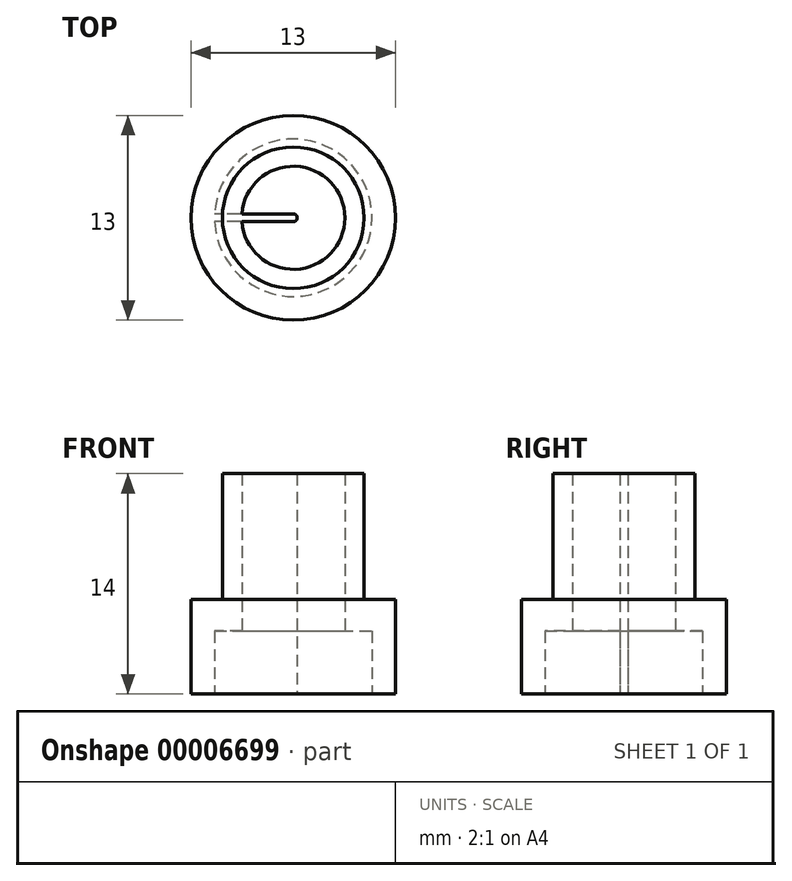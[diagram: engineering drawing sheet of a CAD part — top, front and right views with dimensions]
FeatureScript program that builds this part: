
annotation { "Feature Type Name" : "Feature", "Feature Type Description" : "" }
export const myFeature = defineFeature(function(context is Context, id is Id, definition is map)
    precondition{}
    {
        {
            var Q0;
            Q0=qCreatedBy(makeId("Top.planeOp"),FACE);
            var sketch = newSketch(context, id + "F0", { "sketchPlane" : qUnion([Q0])});
            skCircle(sketch, "E0", {"center": v(0, 0) * mm, "radius": 6.5 * mm});
            skCircle(sketch, "E1", {"center": v(0, 0) * mm, "radius": 5 * mm});
            skSolve(sketch);
        }
        {
            var Q0;
            Q0 = qSketchRegion(id + "F0", true);
            extrude(context, id + "F1", {"entities" : qUnion([Q0]), "depth" : 4 * mm});
        }
        {
            var Q0;
            Q0=makeQuery(id+"F1.opExtrude","CAP_FACE",FACE,{"disambiguationData":[OSD([sQuery(id+"F0.wireOp",EDGE,"E0"),sQuery(id+"F0.wireOp",EDGE,"E1")])],"isStart":false});
            var sketch = newSketch(context, id + "F2", { "sketchPlane" : qUnion([Q0])});
            skCircle(sketch, "E2", {"center": v(0, 0) * mm, "radius": 4.5 * mm});
            skCircle(sketch, "E3", {"center": v(0, 0) * mm, "radius": 3.28 * mm});
            skSolve(sketch);
        }
        {
            var Q0;
            Q0=makeQuery(id+"F2.imprint","IMPRINT",FACE,{"disambiguationData":[TD([[makeQuery(id+"F2.imprint","IMPRINT",EDGE,{"derivedFrom":makeQuery(id+"F1.opExtrude","CAP_EDGE",EDGE,{"disambiguationData":[OSD([sQuery(id+"F0.wireOp",EDGE,"E0")])],"isStart":false})}),1.0]])]});
            var Q1;
            Q1=makeQuery(id+"F2.imprint","IMPRINT",FACE,{"disambiguationData":[TD([[makeQuery(id+"F2.imprint","IMPRINT",EDGE,{"derivedFrom":sQuery(id+"F2.wireOp",EDGE,"E2")}),-1.0]])]});
            extrude(context, id + "F3", {"entities" : qUnion([Q0, Q1]), "operationType" : NewBodyOperationType.ADD, "depth" : 2 * mm});
        }
        {
            var Q0;
            Q0 = qSketchRegion(id + "F2", true);
            extrude(context, id + "F4", {"entities" : qUnion([Q0]), "operationType" : NewBodyOperationType.ADD, "depth" : 10 * mm});
        }
        {
            var Q0;
            Q0=makeQuery(id+"F1.opExtrude","CAP_FACE",FACE,{"disambiguationData":[OSD([sQuery(id+"F0.wireOp",EDGE,"E0"),sQuery(id+"F0.wireOp",EDGE,"E1")])],"isStart":true});
            var sketch = newSketch(context, id + "F5", { "sketchPlane" : qUnion([Q0])});
            skCircle(sketch, "E4", {"center": v(0, 0) * mm, "radius": 0.25 * mm});
            skLineSegment(sketch, "E5.bottom", {"start": v(0, 0.25) * mm, "end": v(-6.5, 0.25) * mm});
            skLineSegment(sketch, "E5.top", {"start": v(0, -0.25) * mm, "end": v(-6.5, -0.25) * mm});
            skLineSegment(sketch, "E5.left", {"start": v(0, 0.25) * mm, "end": v(0, -0.25) * mm});
            skLineSegment(sketch, "E5.right", {"start": v(-6.5, 0.25) * mm, "end": v(-6.5, -0.25) * mm});
            skCircle(sketch, "E6.0", {"center": v(0, 0) * mm, "radius": 3.28 * mm});
            skSolve(sketch);
        }
        {
            var Q0;
            {var subQ0=sQuery(id+"F5.wireOp",EDGE,"E6.0");var subQ3=sQuery(id+"F5.wireOp",EDGE,"E5.bottom");var subQ4=makeQuery(id+"F5.imprint","INTERSECT",VERTEX,{"derivedFrom":[subQ3,subQ0]});Q0=makeQuery(id+"F5.imprint","IMPRINT",FACE,{"disambiguationData":[TD([[makeQuery(id+"F5.imprint","IMPRINT",EDGE,{"disambiguationData":[TD([[subQ4,-1.0]])],"derivedFrom":subQ0}),1.0]])]});}
            var Q1;
            {var subQ0=sQuery(id+"F5.wireOp",EDGE,"E5.left");Q1=makeQuery(id+"F5.imprint","IMPRINT",FACE,{"disambiguationData":[TD([[makeQuery(id+"F5.imprint","IMPRINT",EDGE,{"derivedFrom":subQ0}),-1.0]])]});}
            var Q2;
            {var subQ0=sQuery(id+"F5.wireOp",EDGE,"E5.left");Q2=makeQuery(id+"F5.imprint","IMPRINT",FACE,{"disambiguationData":[TD([[makeQuery(id+"F5.imprint","IMPRINT",EDGE,{"derivedFrom":subQ0}),1.0]])]});}
            var Q3;
            Q3=makeQuery(id+"F4.opExtrude","CAP_FACE",FACE,{"disambiguationData":[OSD([sQuery(id+"F2.wireOp",EDGE,"E2"),sQuery(id+"F2.wireOp",EDGE,"E3")])],"isStart":false});
            extrude(context, id + "F6", {"entities" : qUnion([Q0, Q1, Q2]), "operationType" : NewBodyOperationType.ADD, "endBound" : BoundingType.UP_TO_SURFACE, "oppositeDirection" : true, "endBoundEntityFace" : qUnion([Q3]), "depth" : 25 * mm});
        }
        {
            var Q0;
            {var subQ3=sQuery(id+"F5.wireOp",EDGE,"E5.bottom");var subQ5=sQuery(id+"F5.wireOp",EDGE,"E6.0");var subQ7=makeQuery(id+"F5.imprint","INTERSECT",VERTEX,{"derivedFrom":[subQ3,subQ5]});Q0=makeQuery(id+"F5.imprint","IMPRINT",FACE,{"disambiguationData":[TD([[makeQuery(id+"F5.imprint","IMPRINT",EDGE,{"disambiguationData":[TD([[subQ7,-1.0]])],"derivedFrom":subQ3}),1.0]])]});}
            var Q1;
            {var subQ0=sQuery(id+"F2.wireOp",EDGE,"E2");Q1=makeQuery(id+"F4.boolean.opBoolean","MERGE",FACE,{"derivedFrom":[makeQuery(id+"F3.opExtrude","CAP_FACE",FACE,{"disambiguationData":[OSD([sQuery(id+"F0.wireOp",EDGE,"E0"),subQ0])],"isStart":true}),makeQuery(id+"F4.opExtrude","CAP_FACE",FACE,{"disambiguationData":[OSD([subQ0,sQuery(id+"F2.wireOp",EDGE,"E3")])],"isStart":true})]});}
            extrude(context, id + "F7", {"entities" : qUnion([Q0]), "operationType" : NewBodyOperationType.ADD, "endBound" : BoundingType.UP_TO_SURFACE, "oppositeDirection" : true, "endBoundEntityFace" : qUnion([Q1]), "depth" : 25 * mm});
        }
    });
